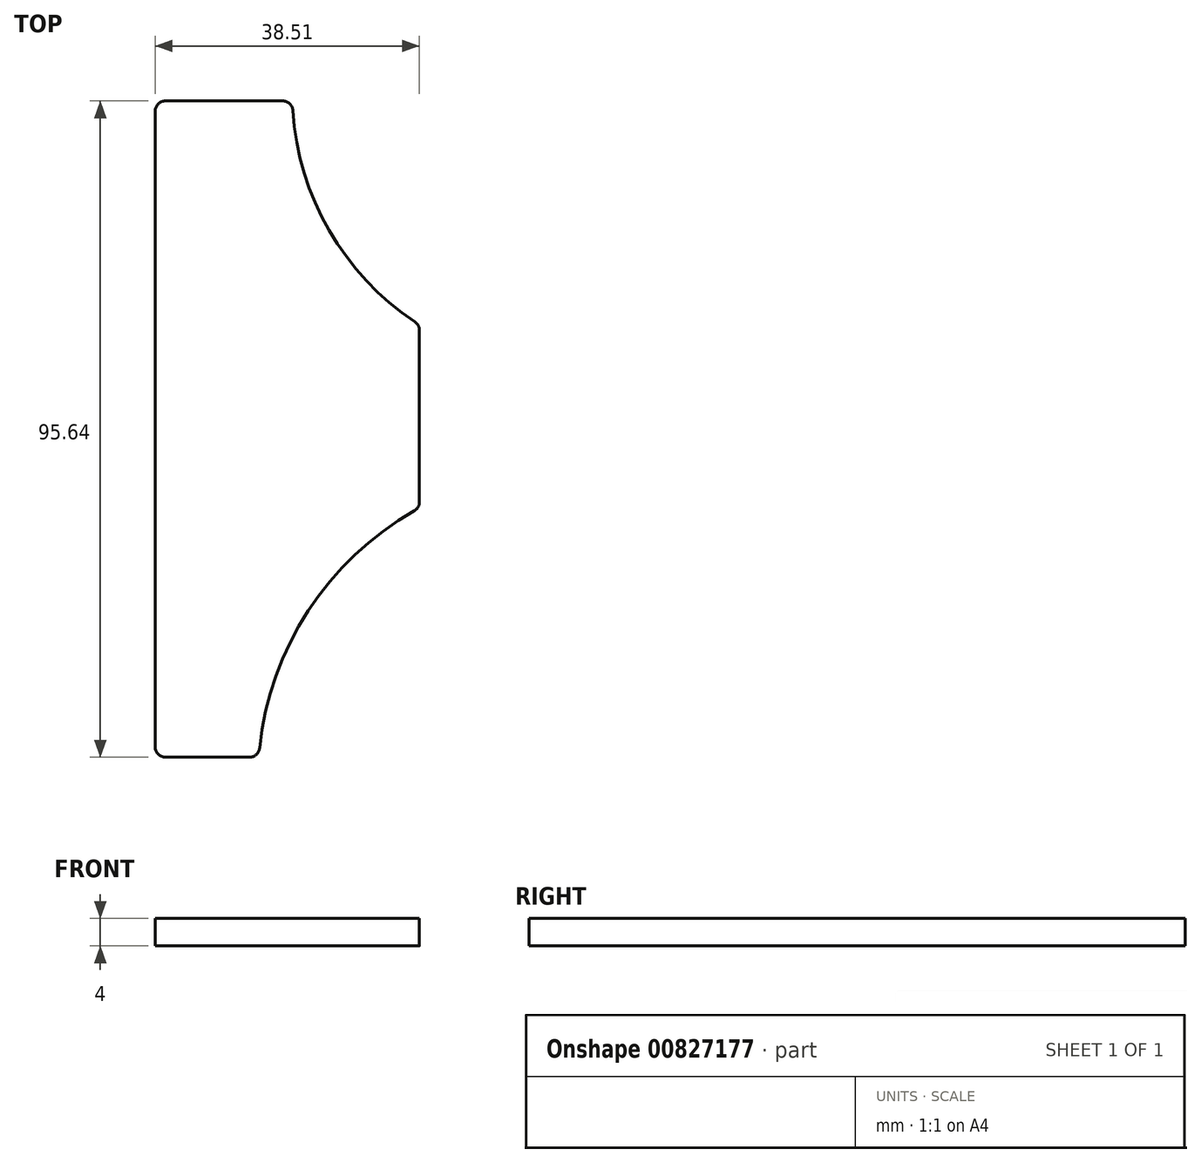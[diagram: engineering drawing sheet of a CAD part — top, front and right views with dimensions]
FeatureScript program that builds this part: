
annotation { "Feature Type Name" : "Feature", "Feature Type Description" : "" }
export const myFeature = defineFeature(function(context is Context, id is Id, definition is map)
    precondition{}
    {
        {
            var Q0;
            Q0=qCreatedBy(makeId("Top.planeOp"),FACE);
            var sketch = newSketch(context, id + "F0", { "sketchPlane" : qUnion([Q0])});
            skArc(sketch, "E0", {"start": v(20, 93.6) * mm, "mid": v(25.3, 76.13) * mm, "end": v(37.78, 62.83) * mm});
            skArc(sketch, "E1", {"start": v(37.7, 35.26) * mm, "mid": v(22.24, 20.73) * mm, "end": v(15.16, 0.72) * mm});
            skLineSegment(sketch, "E2", {"start": v(38.45, 61.58) * mm, "end": v(38.45, 36.57) * mm});
            skLineSegment(sketch, "E3", {"start": v(18.51, 95) * mm, "end": v(1.44, 95) * mm});
            skLineSegment(sketch, "E4", {"start": v(-0.06, 93.5) * mm, "end": v(-0.06, 0.87) * mm});
            skLineSegment(sketch, "E5", {"start": v(13.67, -0.63) * mm, "end": v(1.44, -0.63) * mm});
            skPoint(sketch, "E6.visualSharp", {"position": v(-0.06, 95) * mm});
            skArc(sketch, "E6.filletArc", {"start": v(1.44, 95) * mm, "mid": v(0.38, 94.57) * mm, "end": v(-0.06, 93.5) * mm});
            skPoint(sketch, "E7.visualSharp", {"position": v(19.94, 95) * mm});
            skArc(sketch, "E7.filletArc", {"start": v(20, 93.6) * mm, "mid": v(19.54, 94.6) * mm, "end": v(18.51, 95) * mm});
            skPoint(sketch, "E8.visualSharp", {"position": v(38.45, 62.4) * mm});
            skArc(sketch, "E8.filletArc", {"start": v(38.45, 61.58) * mm, "mid": v(38.28, 62.29) * mm, "end": v(37.78, 62.83) * mm});
            skPoint(sketch, "E9.visualSharp", {"position": v(38.45, 35.68) * mm});
            skArc(sketch, "E9.filletArc", {"start": v(37.7, 35.26) * mm, "mid": v(38.25, 35.81) * mm, "end": v(38.45, 36.57) * mm});
            skPoint(sketch, "E10.visualSharp", {"position": v(-0.06, -0.63) * mm});
            skArc(sketch, "E10.filletArc", {"start": v(-0.06, 0.87) * mm, "mid": v(0.38, -0.19) * mm, "end": v(1.44, -0.63) * mm});
            skPoint(sketch, "E11.visualSharp", {"position": v(15.04, -0.63) * mm});
            skArc(sketch, "E11.filletArc", {"start": v(13.67, -0.63) * mm, "mid": v(14.67, -0.24) * mm, "end": v(15.16, 0.72) * mm});
            skSolve(sketch);
        }
        {
            var Q0;
            Q0=makeQuery(id+"F0.imprint","IMPRINT",FACE,{"disambiguationData":[TD([[makeQuery(id+"F0.imprint","IMPRINT",EDGE,{"derivedFrom":sQuery(id+"F0.wireOp",EDGE,"E0")}),-1.0]])]});
            extrude(context, id + "F1", {"entities" : qUnion([Q0]), "depth" : 4 * mm, "offsetDistance" : 25 * mm});
        }
    });
